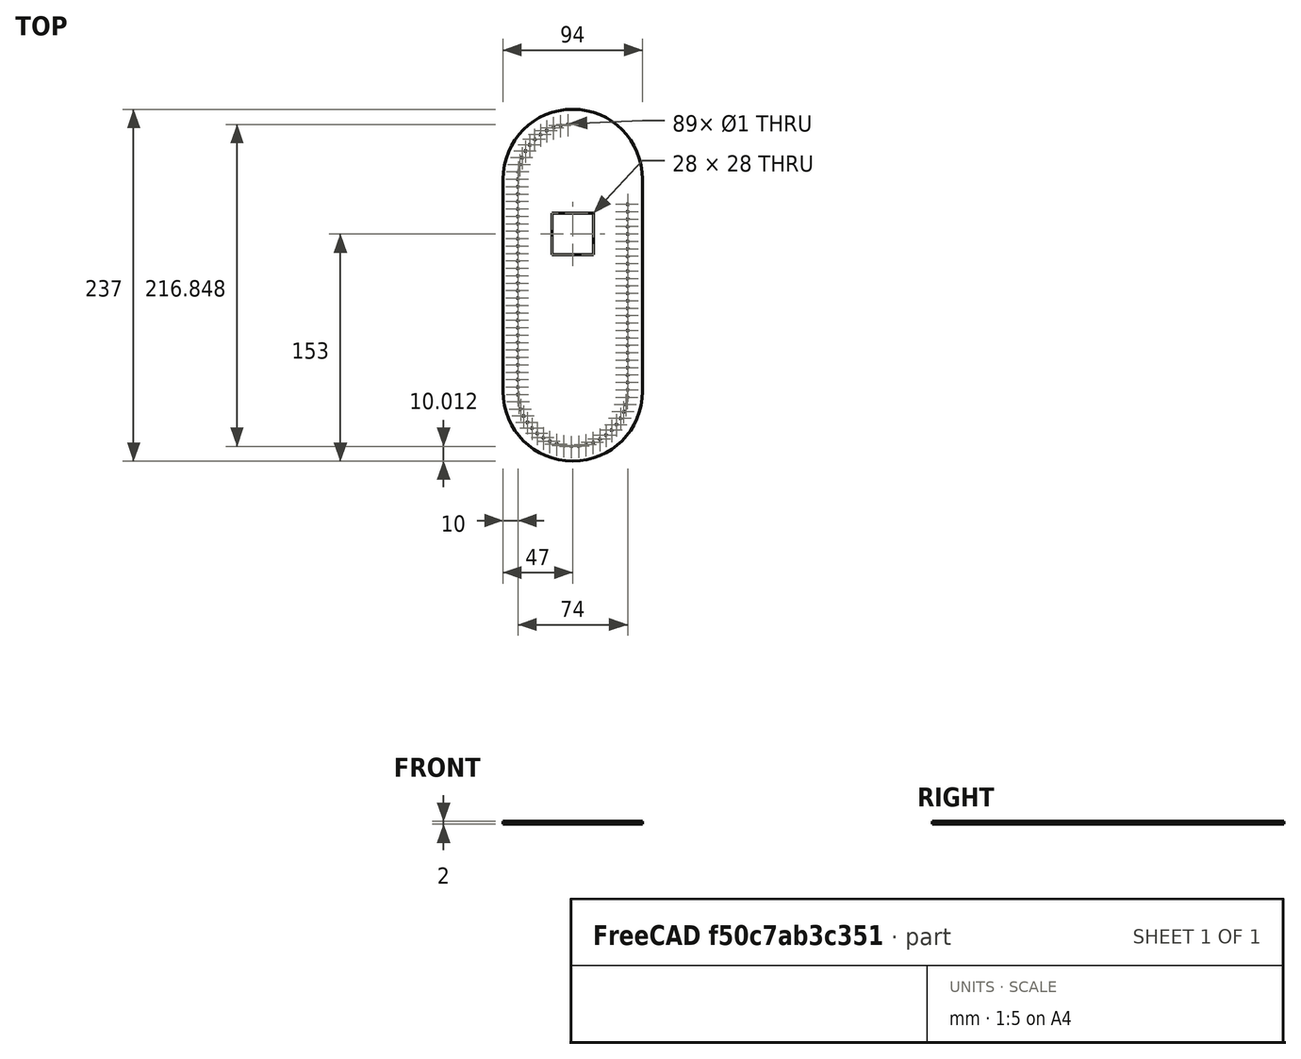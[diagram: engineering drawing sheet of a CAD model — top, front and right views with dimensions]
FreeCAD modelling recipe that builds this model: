
FCSTD DOCUMENT  (FreeCAD 0.18R16146 (Git))
Label: Cote
License: All rights reserved
LicenseURL: http://en.wikipedia.org/wiki/All_rights_reserved
objects: Sketcher::SketchObject×1, PartDesign::Pad×1, PartDesign::Body×1, Drawing::FeatureViewPart×1, Drawing::FeaturePage×1
note: 4 computed .brp shape members not serialized (recipe doc carries the construction recipe); baked Part::Feature solids carry a one-line shape summary decoded from their .brp

FEATURE [Sketcher::SketchObject] Sketch
  MapMode = 5
  Support = -> [XY_Plane]
  sketch-geometry (104):
    g0: LineSegment [constr] StartX=0 StartY=0 StartZ=0 EndX=37 EndY=0 EndZ=0
    g1: LineSegment [constr] StartX=-37 StartY=0 StartZ=0 EndX=0 EndY=0 EndZ=0
    g2: ArcOfCircle [constr] CenterX=0 CenterY=0 CenterZ=0 NormalX=0 NormalY=0 NormalZ=1 AngleXU=0 Radius=37 StartAngle=3.14159 EndAngle=6.28319
    g3: LineSegment [constr] StartX=37 StartY=0 StartZ=0 EndX=37 EndY=143 EndZ=0
    g4: LineSegment [constr] StartX=-37 StartY=0 StartZ=0 EndX=-37 EndY=143 EndZ=0
    g5: LineSegment [constr] StartX=-37 StartY=143 StartZ=0 EndX=37 EndY=143 EndZ=0
    g6: ArcOfCircle [constr] CenterX=0 CenterY=143 CenterZ=0 NormalX=0 NormalY=0 NormalZ=1 AngleXU=0 Radius=37 StartAngle=2.9401e-09 EndAngle=3.14159
    g7: ArcOfCircle CenterX=0 CenterY=0 CenterZ=0 NormalX=0 NormalY=0 NormalZ=1 AngleXU=0 Radius=47 StartAngle=3.14159 EndAngle=6.28319
    g8: ArcOfCircle CenterX=0 CenterY=143 CenterZ=0 NormalX=0 NormalY=0 NormalZ=1 AngleXU=0 Radius=47 StartAngle=2e-16 EndAngle=3.14159
    g9: LineSegment StartX=47 StartY=-1.15e-14 StartZ=0 EndX=47 EndY=143 EndZ=0
    g10: LineSegment StartX=-47 StartY=5.8e-15 StartZ=0 EndX=-47 EndY=143 EndZ=0
    g11: LineSegment StartX=-14 StartY=120 StartZ=0 EndX=14 EndY=120 EndZ=0
    g12: LineSegment StartX=14 StartY=120 StartZ=0 EndX=14 EndY=92 EndZ=0
    g13: LineSegment StartX=14 StartY=92 StartZ=0 EndX=-14 EndY=92 EndZ=0
    g14: LineSegment StartX=-14 StartY=92 StartZ=0 EndX=-14 EndY=120 EndZ=0
    g15: Circle CenterX=37 CenterY=126 CenterZ=0 NormalX=0 NormalY=0 NormalZ=1 AngleXU=0 Radius=0.5
    g16: Circle CenterX=37 CenterY=121 CenterZ=0 NormalX=0 NormalY=0 NormalZ=1 AngleXU=0 Radius=0.5
    g17: Circle CenterX=37 CenterY=111 CenterZ=0 NormalX=0 NormalY=0 NormalZ=1 AngleXU=0 Radius=0.5
    g18: Circle CenterX=37 CenterY=116 CenterZ=0 NormalX=0 NormalY=0 NormalZ=1 AngleXU=0 Radius=0.5
    g19: Circle CenterX=37 CenterY=101 CenterZ=0 NormalX=0 NormalY=0 NormalZ=1 AngleXU=0 Radius=0.5
    g20: Circle CenterX=37 CenterY=106 CenterZ=0 NormalX=0 NormalY=0 NormalZ=1 AngleXU=0 Radius=0.5
    g21: Circle CenterX=37 CenterY=96 CenterZ=0 NormalX=0 NormalY=0 NormalZ=1 AngleXU=0 Radius=0.5
    g22: Circle CenterX=37 CenterY=91 CenterZ=0 NormalX=0 NormalY=0 NormalZ=1 AngleXU=0 Radius=0.5
    g23: Circle CenterX=37 CenterY=86 CenterZ=0 NormalX=0 NormalY=0 NormalZ=1 AngleXU=0 Radius=0.5
    g24: Circle CenterX=37 CenterY=81 CenterZ=0 NormalX=0 NormalY=0 NormalZ=1 AngleXU=0 Radius=0.5
    g25: Circle CenterX=37 CenterY=76 CenterZ=0 NormalX=0 NormalY=0 NormalZ=1 AngleXU=0 Radius=0.5
    g26: Circle CenterX=37 CenterY=71 CenterZ=0 NormalX=0 NormalY=0 NormalZ=1 AngleXU=0 Radius=0.5
    g27: Circle CenterX=37 CenterY=66 CenterZ=0 NormalX=0 NormalY=0 NormalZ=1 AngleXU=0 Radius=0.5
    g28: Circle CenterX=37 CenterY=61 CenterZ=0 NormalX=0 NormalY=0 NormalZ=1 AngleXU=0 Radius=0.5
    g29: Circle CenterX=37 CenterY=56 CenterZ=0 NormalX=0 NormalY=0 NormalZ=1 AngleXU=0 Radius=0.5
    g30: Circle CenterX=37 CenterY=51 CenterZ=0 NormalX=0 NormalY=0 NormalZ=1 AngleXU=0 Radius=0.5
    g31: Circle CenterX=37 CenterY=46 CenterZ=0 NormalX=0 NormalY=0 NormalZ=1 AngleXU=0 Radius=0.5
    g32: Circle CenterX=37 CenterY=41 CenterZ=0 NormalX=0 NormalY=0 NormalZ=1 AngleXU=0 Radius=0.5
    g33: Circle CenterX=37 CenterY=36 CenterZ=0 NormalX=0 NormalY=0 NormalZ=1 AngleXU=0 Radius=0.5
    g34: Circle CenterX=37 CenterY=31 CenterZ=0 NormalX=0 NormalY=0 NormalZ=1 AngleXU=0 Radius=0.5
    g35: Circle CenterX=37 CenterY=26 CenterZ=0 NormalX=0 NormalY=0 NormalZ=1 AngleXU=0 Radius=0.5
    g36: Circle CenterX=37 CenterY=21 CenterZ=0 NormalX=0 NormalY=0 NormalZ=1 AngleXU=0 Radius=0.5
    g37: Circle CenterX=37 CenterY=16 CenterZ=0 NormalX=0 NormalY=0 NormalZ=1 AngleXU=0 Radius=0.5
    g38: Circle CenterX=37 CenterY=11 CenterZ=0 NormalX=0 NormalY=0 NormalZ=1 AngleXU=0 Radius=0.5
    g39: Circle CenterX=37 CenterY=6 CenterZ=0 NormalX=0 NormalY=0 NormalZ=1 AngleXU=0 Radius=0.5
    g40: Circle CenterX=37 CenterY=1 CenterZ=0 NormalX=0 NormalY=0 NormalZ=1 AngleXU=0 Radius=0.5
    g41: Circle CenterX=36.7837 CenterY=-3.99532 CenterZ=0 NormalX=0 NormalY=0 NormalZ=1 AngleXU=0 Radius=0.5
    g42: Circle CenterX=35.9091 CenterY=-8.91824 CenterZ=0 NormalX=0 NormalY=0 NormalZ=1 AngleXU=0 Radius=0.5
    g43: Circle CenterX=34.3788 CenterY=-13.6783 CenterZ=0 NormalX=0 NormalY=0 NormalZ=1 AngleXU=0 Radius=0.5
    g44: Circle CenterX=32.2207 CenterY=-18.1886 CenterZ=0 NormalX=0 NormalY=0 NormalZ=1 AngleXU=0 Radius=0.5
    g45: Circle CenterX=29.4742 CenterY=-22.3667 CenterZ=0 NormalX=0 NormalY=0 NormalZ=1 AngleXU=0 Radius=0.5
    g46: Circle CenterX=26.1895 CenterY=-26.1364 CenterZ=0 NormalX=0 NormalY=0 NormalZ=1 AngleXU=0 Radius=0.5
    g47: Circle CenterX=22.4265 CenterY=-29.4288 CenterZ=0 NormalX=0 NormalY=0 NormalZ=1 AngleXU=0 Radius=0.5
    g48: Circle CenterX=18.2539 CenterY=-32.1837 CenterZ=0 NormalX=0 NormalY=0 NormalZ=1 AngleXU=0 Radius=0.5
    g49: Circle CenterX=13.7481 CenterY=-34.351 CenterZ=0 NormalX=0 NormalY=0 NormalZ=1 AngleXU=0 Radius=0.5
    g50: Circle CenterX=8.99111 CenterY=-35.8909 CenterZ=0 NormalX=0 NormalY=0 NormalZ=1 AngleXU=0 Radius=0.5
    g51: Circle CenterX=4.06997 CenterY=-36.7755 CenterZ=0 NormalX=0 NormalY=0 NormalZ=1 AngleXU=0 Radius=0.5
    g52: Circle CenterX=-0.925498 CenterY=-36.9884 CenterZ=0 NormalX=0 NormalY=0 NormalZ=1 AngleXU=0 Radius=0.5
    g53: Circle CenterX=-5.90406 CenterY=-36.5259 CenterZ=0 NormalX=0 NormalY=0 NormalZ=1 AngleXU=0 Radius=0.5
    g54: Circle CenterX=-10.7748 CenterY=-35.3964 CenterZ=0 NormalX=0 NormalY=0 NormalZ=1 AngleXU=0 Radius=0.5
    g55: Circle CenterX=-15.4488 CenterY=-33.6205 CenterZ=0 NormalX=0 NormalY=0 NormalZ=1 AngleXU=0 Radius=0.5
    g56: Circle CenterX=-19.8406 CenterY=-31.2306 CenterZ=0 NormalX=0 NormalY=0 NormalZ=1 AngleXU=0 Radius=0.5
    g57: Circle CenterX=-23.8702 CenterY=-28.2704 CenterZ=0 NormalX=0 NormalY=0 NormalZ=1 AngleXU=0 Radius=0.5
    g58: Circle CenterX=-27.4638 CenterY=-24.7939 CenterZ=0 NormalX=0 NormalY=0 NormalZ=1 AngleXU=0 Radius=0.5
    g59: Circle CenterX=-30.5559 CenterY=-20.8647 CenterZ=0 NormalX=0 NormalY=0 NormalZ=1 AngleXU=0 Radius=0.5
    g60: Circle CenterX=-33.09 CenterY=-16.5544 CenterZ=0 NormalX=0 NormalY=0 NormalZ=1 AngleXU=0 Radius=0.5
    g61: Circle CenterX=-35.0199 CenterY=-11.9419 CenterZ=0 NormalX=0 NormalY=0 NormalZ=1 AngleXU=0 Radius=0.5
    g62: Circle CenterX=-36.3102 CenterY=-7.11122 CenterZ=0 NormalX=0 NormalY=0 NormalZ=1 AngleXU=0 Radius=0.5
    g63: Circle CenterX=-36.9374 CenterY=-2.15072 CenterZ=0 NormalX=0 NormalY=0 NormalZ=1 AngleXU=0 Radius=0.5
    g64: Circle CenterX=-37 CenterY=2.84889 CenterZ=0 NormalX=0 NormalY=0 NormalZ=1 AngleXU=0 Radius=0.5
    g65: Circle CenterX=-37 CenterY=7.84889 CenterZ=0 NormalX=0 NormalY=0 NormalZ=1 AngleXU=0 Radius=0.5
    g66: Circle CenterX=-37 CenterY=12.8489 CenterZ=0 NormalX=0 NormalY=0 NormalZ=1 AngleXU=0 Radius=0.5
    g67: Circle CenterX=-37 CenterY=17.8489 CenterZ=0 NormalX=0 NormalY=0 NormalZ=1 AngleXU=0 Radius=0.5
    g68: Circle CenterX=-37 CenterY=22.8489 CenterZ=0 NormalX=0 NormalY=0 NormalZ=1 AngleXU=0 Radius=0.5
    g69: Circle CenterX=-37 CenterY=27.8489 CenterZ=0 NormalX=0 NormalY=0 NormalZ=1 AngleXU=0 Radius=0.5
    g70: Circle CenterX=-37 CenterY=32.8489 CenterZ=0 NormalX=0 NormalY=0 NormalZ=1 AngleXU=0 Radius=0.5
    g71: Circle CenterX=-37 CenterY=37.8489 CenterZ=0 NormalX=0 NormalY=0 NormalZ=1 AngleXU=0 Radius=0.5
    g72: Circle CenterX=-37 CenterY=42.8489 CenterZ=0 NormalX=0 NormalY=0 NormalZ=1 AngleXU=0 Radius=0.5
    g73: Circle CenterX=-37 CenterY=47.8489 CenterZ=0 NormalX=0 NormalY=0 NormalZ=1 AngleXU=0 Radius=0.5
    g74: Circle CenterX=-37 CenterY=52.8489 CenterZ=0 NormalX=0 NormalY=0 NormalZ=1 AngleXU=0 Radius=0.5
    g75: Circle CenterX=-37 CenterY=57.8489 CenterZ=0 NormalX=0 NormalY=0 NormalZ=1 AngleXU=0 Radius=0.5
    g76: Circle CenterX=-37 CenterY=62.8489 CenterZ=0 NormalX=0 NormalY=0 NormalZ=1 AngleXU=0 Radius=0.5
    g77: Circle CenterX=-37 CenterY=67.8489 CenterZ=0 NormalX=0 NormalY=0 NormalZ=1 AngleXU=0 Radius=0.5
    g78: Circle CenterX=-37 CenterY=72.8489 CenterZ=0 NormalX=0 NormalY=0 NormalZ=1 AngleXU=0 Radius=0.5
    g79: Circle CenterX=-37 CenterY=77.8489 CenterZ=0 NormalX=0 NormalY=0 NormalZ=1 AngleXU=0 Radius=0.5
    g80: Circle CenterX=-37 CenterY=82.8489 CenterZ=0 NormalX=0 NormalY=0 NormalZ=1 AngleXU=0 Radius=0.5
    g81: Circle CenterX=-37 CenterY=87.8489 CenterZ=0 NormalX=0 NormalY=0 NormalZ=1 AngleXU=0 Radius=0.5
    g82: Circle CenterX=-37 CenterY=92.8489 CenterZ=0 NormalX=0 NormalY=0 NormalZ=1 AngleXU=0 Radius=0.5
    g83: Circle CenterX=-37 CenterY=97.8489 CenterZ=0 NormalX=0 NormalY=0 NormalZ=1 AngleXU=0 Radius=0.5
    g84: Circle CenterX=-37 CenterY=102.849 CenterZ=0 NormalX=0 NormalY=0 NormalZ=1 AngleXU=0 Radius=0.5
    g85: Circle CenterX=-37 CenterY=107.849 CenterZ=0 NormalX=0 NormalY=0 NormalZ=1 AngleXU=0 Radius=0.5
    g86: Circle CenterX=-37 CenterY=112.849 CenterZ=0 NormalX=0 NormalY=0 NormalZ=1 AngleXU=0 Radius=0.5
    g87: Circle CenterX=-37 CenterY=117.849 CenterZ=0 NormalX=0 NormalY=0 NormalZ=1 AngleXU=0 Radius=0.5
    g88: Circle CenterX=-37 CenterY=122.849 CenterZ=0 NormalX=0 NormalY=0 NormalZ=1 AngleXU=0 Radius=0.5
    g89: Circle CenterX=-37 CenterY=127.849 CenterZ=0 NormalX=0 NormalY=0 NormalZ=1 AngleXU=0 Radius=0.5
    g90: Circle CenterX=-37 CenterY=132.849 CenterZ=0 NormalX=0 NormalY=0 NormalZ=1 AngleXU=0 Radius=0.5
    g91: Circle CenterX=-37 CenterY=137.849 CenterZ=0 NormalX=0 NormalY=0 NormalZ=1 AngleXU=0 Radius=0.5
    g92: Circle CenterX=-37 CenterY=142.849 CenterZ=0 NormalX=0 NormalY=0 NormalZ=1 AngleXU=0 Radius=0.5
    g93: Circle CenterX=-36.6822 CenterY=147.839 CenterZ=0 NormalX=0 NormalY=0 NormalZ=1 AngleXU=0 Radius=0.5
    g94: Circle CenterX=-35.6949 CenterY=152.74 CenterZ=0 NormalX=0 NormalY=0 NormalZ=1 AngleXU=0 Radius=0.5
    g95: Circle CenterX=-34.0557 CenterY=157.464 CenterZ=0 NormalX=0 NormalY=0 NormalZ=1 AngleXU=0 Radius=0.5
    g96: Circle CenterX=-31.7946 CenterY=161.924 CenterZ=0 NormalX=0 NormalY=0 NormalZ=1 AngleXU=0 Radius=0.5
    g97: Circle CenterX=-28.9529 CenterY=166.038 CenterZ=0 NormalX=0 NormalY=0 NormalZ=1 AngleXU=0 Radius=0.5
    g98: Circle CenterX=-25.5825 CenterY=169.731 CenterZ=0 NormalX=0 NormalY=0 NormalZ=1 AngleXU=0 Radius=0.5
    g99: Circle CenterX=-21.7449 CenterY=172.936 CenterZ=0 NormalX=0 NormalY=0 NormalZ=1 AngleXU=0 Radius=0.5
    g100: Circle CenterX=-17.5102 CenterY=175.594 CenterZ=0 NormalX=0 NormalY=0 NormalZ=1 AngleXU=0 Radius=0.5
    g101: Circle CenterX=-12.9558 CenterY=177.658 CenterZ=0 NormalX=0 NormalY=0 NormalZ=1 AngleXU=0 Radius=0.5
    g102: Circle CenterX=-8.16472 CenterY=179.088 CenterZ=0 NormalX=0 NormalY=0 NormalZ=1 AngleXU=0 Radius=0.5
    g103: Circle CenterX=-3.22457 CenterY=179.859 CenterZ=0 NormalX=0 NormalY=0 NormalZ=1 AngleXU=0 Radius=0.5
  constraints (311):
    c: Horizontal(g0)
    c: Coincident(g0,g-1)
    c: Horizontal(g1)
    c: Coincident(g1,g0)
    c: DistanceX(g0,g0) = 37
    c: Coincident(g2,g0)
    c: Coincident(g2,g0)
    c: Coincident(g2,g1)
    c: Vertical(g3)
    c: Coincident(g3,g0)
    c: DistanceY(g3,g3) = 143
    c: Coincident(g4,g1)
    c: Vertical(g4)
    c: DistanceY(g4,g4) = 143
    c: Coincident(g5,g4)
    c: Coincident(g5,g3)
    c: PointOnObject(g6,g-2)
    c: PointOnObject(g6,g5)
    c: Coincident(g6,g4)
    c: PointOnObject(g6,g3)
    c: Coincident(g7,g-1)
    c: PointOnObject(g7,g-1)
    c: PointOnObject(g7,g-1)
    c: Radius(g7) = 47
    c: Coincident(g8,g6)
    c: PointOnObject(g8,g5)
    c: PointOnObject(g8,g5)
    c: Radius(g8) = 47
    c: Coincident(g9,g7)
    c: Coincident(g9,g8)
    c: Coincident(g10,g7)
    c: Coincident(g10,g8)
    c: Coincident(g11,g12)
    c: Coincident(g12,g13)
    c: Coincident(g13,g14)
    c: Coincident(g14,g11)
    c: Horizontal(g11)
    c: Horizontal(g13)
    c: Vertical(g12)
    c: Vertical(g14)
    c: Distance(g11,g5) = 23
    c: DistanceY(g14,g14) = 28
    c: DistanceX(g11,g11) = 28
    c: DistanceX(g-2,g11) = -14
    c: Radius(g15) = 0.5
    c: PointOnObject(g15,g3)
    c: Distance(g15,g5) = 17
    c: PointOnObject(g16,g3)
    c: PointOnObject(g17,g3)
    c: PointOnObject(g18,g3)
    c: PointOnObject(g19,g3)
    c: PointOnObject(g20,g3)
    c: Radius(g20) = 0.5
    c: Radius(g19) = 0.5
    c: Radius(g18) = 0.5
    c: Radius(g17) = 0.5
    c: Radius(g16) = 0.5
    c: Distance(g16,g15) = 5
    c: Distance(g18,g16) = 5
    c: Distance(g17,g18) = 5
    c: Distance(g20,g17) = 5
    c: Distance(g19,g20) = 5
    c: PointOnObject(g21,g3)
    c: Radius(g21) = 0.5
    c: Distance(g21,g19) = 5
    c: PointOnObject(g22,g3)
    c: Radius(g22) = 0.5
    c: Distance(g22,g21) = 5
    c: PointOnObject(g23,g3)
    c: Radius(g23) = 0.5
    c: Distance(g23,g22) = 5
    c: PointOnObject(g24,g3)
    c: Radius(g24) = 0.5
    c: Distance(g24,g23) = 5
    c: PointOnObject(g25,g3)
    c: Radius(g25) = 0.5
    c: Distance(g25,g24) = 5
    c: PointOnObject(g26,g3)
    c: PointOnObject(g27,g3)
    c: Radius(g26) = 0.5
    c: Radius(g27) = 0.5
    c: Distance(g26,g25) = 5
    c: Distance(g27,g26) = 5
    c: PointOnObject(g28,g3)
    c: PointOnObject(g29,g3)
    c: Radius(g29) = 0.5
    c: Radius(g28) = 0.5
    c: Distance(g28,g27) = 5
    c: Distance(g29,g28) = 5
    c: PointOnObject(g30,g3)
    c: PointOnObject(g31,g3)
    c: PointOnObject(g32,g3)
    c: PointOnObject(g33,g3)
    c: Radius(g30) = 0.5
    c: Radius(g31) = 0.5
    c: Radius(g32) = 0.5
    c: Radius(g33) = 0.5
    c: Distance(g30,g29) = 5
    c: Distance(g31,g30) = 5
    c: Distance(g32,g31) = 5
    c: Distance(g33,g32) = 5
    c: PointOnObject(g34,g3)
    c: PointOnObject(g35,g3)
    c: PointOnObject(g36,g3)
    c: PointOnObject(g37,g3)
    c: Radius(g34) = 0.5
    c: Radius(g35) = 0.5
    c: Radius(g36) = 0.5
    c: Radius(g37) = 0.5
    c: Distance(g34,g33) = 5
    c: Distance(g35,g34) = 5
    c: Distance(g36,g35) = 5
    c: Distance(g37,g36) = 5
    c: PointOnObject(g38,g3)
    c: PointOnObject(g39,g3)
    c: PointOnObject(g40,g3)
    c: Radius(g38) = 0.5
    c: Radius(g39) = 0.5
    c: Radius(g40) = 0.5
    c: Distance(g38,g37) = 5
    c: Distance(g39,g38) = 5
    c: Distance(g40,g39) = 5
    c: PointOnObject(g41,g2)
    c: PointOnObject(g42,g2)
    c: PointOnObject(g43,g2)
    c: PointOnObject(g44,g2)
    c: PointOnObject(g45,g2)
    c: Radius(g41) = 0.5
    c: Radius(g42) = 0.5
    c: Radius(g43) = 0.5
    c: Radius(g44) = 0.5
    c: Radius(g45) = 0.5
    c: Distance(g45,g44) = 5
    c: Distance(g44,g43) = 5
    c: Distance(g43,g42) = 5
    c: Distance(g42,g41) = 5
    c: Distance(g41,g40) = 5
    c: PointOnObject(g46,g2)
    c: PointOnObject(g47,g2)
    c: PointOnObject(g48,g2)
    c: PointOnObject(g49,g2)
    c: Radius(g46) = 0.5
    c: Radius(g47) = 0.5
    c: Radius(g48) = 0.5
    c: Radius(g49) = 0.5
    c: Distance(g49,g48) = 5
    c: Distance(g48,g47) = 5
    c: Distance(g47,g46) = 5
    c: Distance(g46,g45) = 5
    c: PointOnObject(g50,g2)
    c: PointOnObject(g51,g2)
    c: PointOnObject(g52,g2)
    c: PointOnObject(g53,g2)
    c: PointOnObject(g54,g2)
    c: PointOnObject(g55,g2)
    c: PointOnObject(g56,g2)
    c: PointOnObject(g57,g2)
    c: Radius(g57) = 0.5
    c: Radius(g56) = 0.5
    c: Radius(g55) = 0.5
    c: Radius(g54) = 0.5
    c: Radius(g53) = 0.5
    c: Radius(g52) = 0.5
    c: Radius(g51) = 0.5
    c: Radius(g50) = 0.5
    c: Distance(g50,g49) = 5
    c: Distance(g51,g50) = 5
    c: Distance(g52,g51) = 5
    c: Distance(g53,g52) = 5
    c: Distance(g54,g53) = 5
    c: Distance(g57,g56) = 5
    c: Distance(g56,g55) = 5
    c: Distance(g55,g54) = 5
    c: PointOnObject(g58,g2)
    c: PointOnObject(g59,g2)
    c: PointOnObject(g60,g2)
    c: PointOnObject(g61,g2)
    c: PointOnObject(g62,g2)
    c: Radius(g62) = 0.5
    c: Radius(g61) = 0.5
    c: Radius(g60) = 0.5
    c: Radius(g59) = 0.5
    c: Radius(g58) = 0.5
    c: Distance(g58,g57) = 5
    c: Distance(g58,g59) = 5
    c: Distance(g60,g59) = 5
    c: Distance(g61,g60) = 5
    c: Distance(g61,g62) = 5
    c: PointOnObject(g63,g2)
    c: Radius(g63) = 0.5
    c: Distance(g63,g62) = 5
    c: PointOnObject(g64,g4)
    c: PointOnObject(g65,g4)
    c: PointOnObject(g66,g4)
    c: PointOnObject(g67,g4)
    c: PointOnObject(g68,g4)
    c: PointOnObject(g69,g4)
    c: PointOnObject(g70,g4)
    c: PointOnObject(g71,g4)
    c: PointOnObject(g72,g4)
    c: PointOnObject(g73,g4)
    c: Radius(g73) = 0.5
    c: Radius(g72) = 0.5
    c: Radius(g71) = 0.5
    c: Radius(g70) = 0.5
    c: Radius(g69) = 0.5
    c: Radius(g68) = 0.5
    c: Radius(g67) = 0.5
    c: Radius(g66) = 0.5
    c: Radius(g65) = 0.5
    c: Radius(g64) = 0.5
    c: Distance(g73,g72) = 5
    c: Distance(g72,g71) = 5
    c: Distance(g71,g70) = 5
    c: Distance(g70,g69) = 5
    c: Distance(g69,g68) = 5
    c: Distance(g68,g67) = 5
    c: Distance(g67,g66) = 5
    c: Distance(g66,g65) = 5
    c: Distance(g65,g64) = 5
    c: Distance(g64,g63) = 5
    c: PointOnObject(g74,g4)
    c: PointOnObject(g75,g4)
    c: PointOnObject(g76,g4)
    c: PointOnObject(g77,g4)
    c: PointOnObject(g78,g4)
    c: PointOnObject(g80,g4)
    c: PointOnObject(g81,g4)
    c: PointOnObject(g82,g4)
    c: PointOnObject(g83,g4)
    c: PointOnObject(g79,g4)
    c: Radius(g74) = 0.5
    c: Radius(g75) = 0.5
    c: Radius(g76) = 0.5
    c: Radius(g77) = 0.5
    c: Radius(g78) = 0.5
    c: Radius(g79) = 0.5
    c: Radius(g80) = 0.5
    c: Radius(g81) = 0.5
    c: Radius(g82) = 0.5
    c: Radius(g83) = 0.5
    c: Distance(g82,g83) = 5
    c: Distance(g82,g81) = 5
    c: Distance(g81,g80) = 5
    c: Distance(g80,g79) = 5
    c: Distance(g79,g78) = 5
    c: Distance(g78,g77) = 5
    c: Distance(g77,g76) = 5
    c: Distance(g76,g75) = 5
    c: Distance(g75,g74) = 5
    c: Distance(g74,g73) = 5
    c: PointOnObject(g84,g4)
    c: PointOnObject(g85,g4)
    c: PointOnObject(g86,g4)
    c: PointOnObject(g87,g4)
    c: PointOnObject(g88,g4)
    c: PointOnObject(g89,g4)
    c: PointOnObject(g90,g4)
    c: PointOnObject(g91,g4)
    c: Radius(g91) = 0.5
    c: Radius(g90) = 0.5
    c: Radius(g89) = 0.5
    c: Radius(g88) = 0.5
    c: Radius(g87) = 0.5
    c: Radius(g86) = 0.5
    c: Radius(g85) = 0.5
    c: Radius(g84) = 0.5
    c: Distance(g83,g84) = 5
    c: Distance(g84,g85) = 5
    c: Distance(g85,g86) = 5
    c: Distance(g86,g87) = 5
    c: Distance(g87,g88) = 5
    c: Distance(g88,g89) = 5
    c: Distance(g89,g90) = 5
    c: Distance(g90,g91) = 5
    c: PointOnObject(g92,g4)
    c: Radius(g92) = 0.5
    c: Distance(g91,g92) = 5
    c: PointOnObject(g93,g6)
    c: PointOnObject(g94,g6)
    c: PointOnObject(g95,g6)
    c: PointOnObject(g96,g6)
    c: PointOnObject(g97,g6)
    c: PointOnObject(g98,g6)
    c: PointOnObject(g99,g6)
    c: PointOnObject(g100,g6)
    c: PointOnObject(g101,g6)
    c: PointOnObject(g102,g6)
    c: Radius(g102) = 0.5
    c: Radius(g101) = 0.5
    c: Radius(g100) = 0.5
    c: Radius(g99) = 0.5
    c: Radius(g98) = 0.5
    c: Radius(g97) = 0.5
    c: Radius(g96) = 0.5
    c: Radius(g95) = 0.5
    c: Radius(g94) = 0.5
    c: Radius(g93) = 0.5
    c: Distance(g102,g101) = 5
    c: Distance(g100,g101) = 5
    c: Distance(g100,g99) = 5
    c: Distance(g98,g99) = 5
    c: Distance(g98,g97) = 5
    c: Distance(g96,g97) = 5
    c: Distance(g95,g96) = 5
    c: Distance(g95,g94) = 5
    c: Distance(g94,g93) = 5
    c: Distance(g93,g92) = 5
    c: PointOnObject(g103,g6)
    c: Radius(g103) = 0.5
    c: Distance(g103,g102) = 5
FEATURE [PartDesign::Pad] Pad
  Length = 2
  Length2 = 100
  Profile = -> Sketch
  Type = 0
FEATURE [PartDesign::Body] Body
  Group = -> [Sketch,Pad]
  Origin = -> Origin
  Tip = -> Pad
FEATURE [Drawing::FeatureViewPart] Ortho  label="Ortho_0_0"
  Direction = (0,0,1)
  HiddenWidth = 0.15
  LineWidth = 0.35
  Rotation = 90
  ShowHiddenLines = false
  ShowSmoothLines = false
  Source = -> Pad
  Tolerance = 0.05
  ViewResult = <blob: 4462 chars omitted>
  Visible = false
  X = 77
  Y = 86
FEATURE [Drawing::FeaturePage] Page
  EditableTexts = Dubois Jérôme | Côté | FreeCAD DRAWING | A4 | 1/1 | 1 | PN | DN | 28/12/2021 | REV A
  Group = -> [Ortho]
  Template = <path>
note: 1 file-system path scrubbed to <path> (originals preserved in the JSON sidecar)
